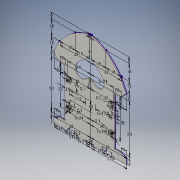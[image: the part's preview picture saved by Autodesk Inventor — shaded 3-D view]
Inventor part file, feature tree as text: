
AUTODESK INVENTOR PART (.ipt)
format: ipt  version: 2016 (Build 200138000, 138)  size: 406,528 bytes
history: native  units: mm
features: other x6, extrude x2, sketch x2, projected_geometry x1
ambient origin geometry x8: Origin, YZ Plane, XZ Plane, XY Plane, X Axis, Y Axis, Z Axis, Center Point
bodies: Body1 (feature_tree)
feature tree (11):
  other  "shitaita"
  other  "肉抜き"
  other  "作業平面1"
  other  "スペード"
  other  "作業平面3"
  extrude  "押し出し9"  Depth=50.0mm
  sketch  "スケッチ17"
  extrude  "押し出し10"  Depth=26.0mm
  sketch  "スケッチ13"
  projected_geometry  "投影ループ6"
  other  "イメージ9"
